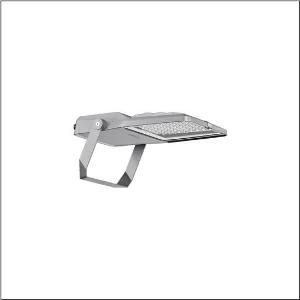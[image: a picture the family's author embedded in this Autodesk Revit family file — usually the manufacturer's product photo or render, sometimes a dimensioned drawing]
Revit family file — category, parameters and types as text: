
# Revit family: floodlight_fl_21_mini___pl61_5xa7773c4c1a_fa47
name_source: partatom
category: Lighting Fixtures
units: mm (PartAtom-declared; Revit-internal decimal feet)

## family parameters
Cut with Voids When Loaded = No
Host = Face
Light Source = No
Part Type = Normal
Room Calculation Point = No
Round Connector Dimension = Use Diameter
Shared = No

## types (1)
- --- (1 x LED, 19990 lm, 163.5 W, 4000K)
    Apparent Load = 163 VA
    CIE Flux Codes = 33 65 98 100 100
    Color Rendering = 70
    Color Temperature = 4000K
    Default Elevation = 1800 mm
    Description = Floodlight FL 21 mini, floodlight, primary light control with lens, of PMMA, primary optical cover: protective disc, of toughened safety glass, transparent, light distribution: PL61, light emission: direct distribution, installation type: surface-mounted, LED, High Power LED, rated luminous flux: 19.990lm, luminous efficacy: 122lm/W, light colour: 740, colour temperature: 4000K, control: Temp-Guard, with terminal, 6-pole, mains connection: 220..240V, AC, 50/60Hz, start of lifetime: 164W, luminaire housing, of diecast aluminium, powder-coated, Siteco® metallic grey (DB 702S), corrosivity category C5 mid according to DIN EN ISO 12944, sealing non-destructively replaceable, mounting bracket, of steel, galvanised, powder-coated, Siteco® metallic grey (DB 702S), ON/OFF, protection rating (complete): IP66, insulation class (complete): insulation class I (protective earthing), certification: CE, ENEC, VDE, protection symbol: D, impact resistance: IK08, permissible operating ambient temperature: -40..+40°C, permissible operating ambient temperature for outdoor applications: -40..+50°C, standard: DIN EN 12944, LABS conformity tested according to VDMA 24364:2018-05, packaging unit: 1 piece

Light Distribution: PL61
    Height = 70 mm
    Lamp = 1 x LED
    Lamp Light Flux = 19990 lm
    Lamp Power = 163.5 W
    Lamp count = 1
    Length = 485 mm
    Luminous efficacy = 122 lm/W
    Manufacturer = Siteco
    ModVariant = No
    Model = 5XA7773C4C1A
    Number of Poles = 1
    OnlyDefault = Yes
    Power Factor = 1
    Product Name = Floodlight FL 21 mini | PL61
    Product group = floodlight | pylon annexe
    ProductGroupID = 6200
    Protection Class = Protection class I
    Protection Degree = IP 66
    RLX_Detail_Level = 1
    RLX_Emergency_Light_Flux = 0 lm
    RLX_Emergency_Type = 0
    RLX_Emergency_Type_DB = No
    RlxData = <blob elided: 94201 chars, md5=c3b5055b>
    Socket = socket
    Standby Power = 0 W
    System Light Flux = 19990 lm
    System Power = 163 W
    Type Comments = factory setting: luminous flux: 100 % | (ON | - | - | - | - | - | - | -) | 825 mA
    Type Image = l_1006845.jpg
    URL = http://relux.com
    VarID = @adj_105907
    Voltage = 0 V
    Weight = 0.00 kg
    Width = 337 mm

## geometry (parser evidence)
native form markers: Blend x4, Sweep x15
no freeform markers — native parametric forms only
